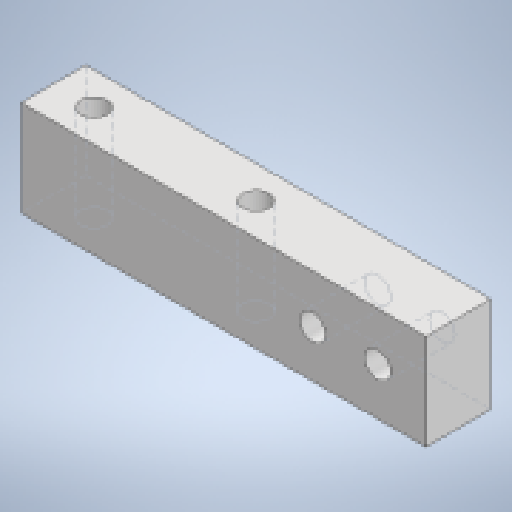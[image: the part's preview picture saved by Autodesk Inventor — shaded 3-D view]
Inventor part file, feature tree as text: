
AUTODESK INVENTOR PART (.ipt)
format: ipt  version: 2023 (Build 270158000, 158)  size: 160,256 bytes
history: native  units: mm
features: extrude x4, sketch x4
ambient origin geometry x8: Origin, YZ Plane, XZ Plane, XY Plane, X Axis, Y Axis, Z Axis, Center Point
bodies: Solid1 (feature_tree)
feature tree (8):
  extrude  "Extrusion1"  Depth=15.0mm
  extrude  "Extrusion2"  Depth=10.0mm
  extrude  "Extrusion3"  Depth=2.0mm
  extrude  "Extrusion4"  Depth=4.0mm
  sketch  "Sketch1"  dims[d0=5.9mm d1=15.0mm]
  sketch  "Sketch2"  dims[d2=4.0mm d3=0.0mm d4=10.0mm]
  sketch  "Sketch3"  dims[d5=2.5mm d6=2.0mm]
  sketch  "Sketch4"  dims[d7=2.0mm d8=1.6mm d9=1.6mm d10=8.0mm d11=0.0mm d12=10.0mm d13=4.0mm d14=0.0mm d15=1.6mm d16=5.9mm d17=4.0mm d18=4.0mm d19=4.0mm d20=3.0mm d21=1.6mm d22=1.6mm d23=4.0mm d24=0.0mm]
